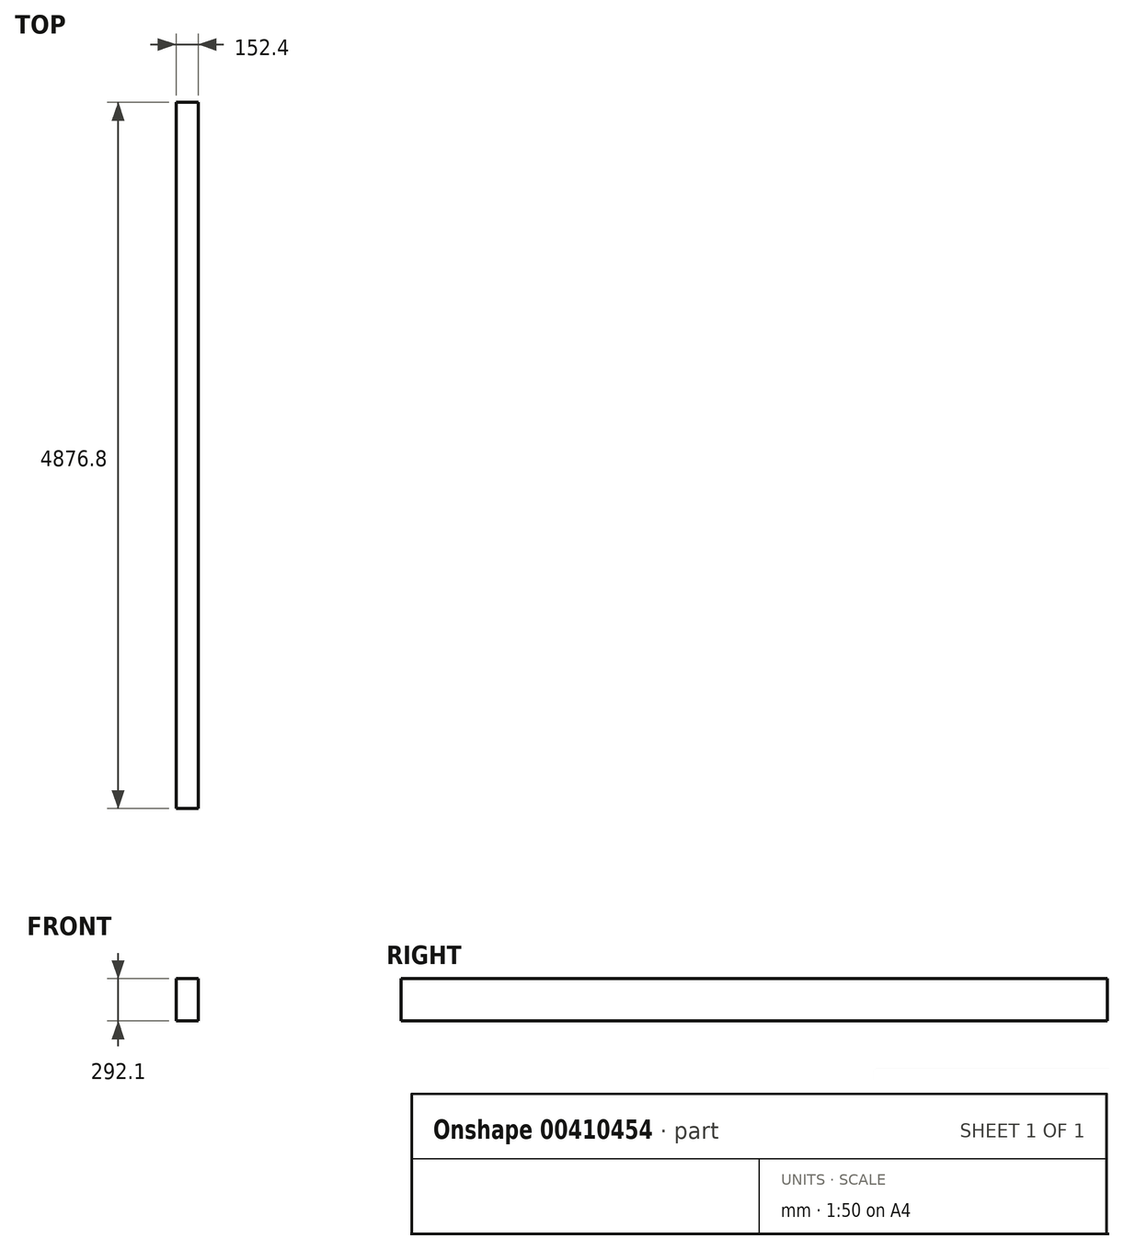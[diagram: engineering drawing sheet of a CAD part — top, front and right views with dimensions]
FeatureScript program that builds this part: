
annotation { "Feature Type Name" : "Feature", "Feature Type Description" : "" }
export const myFeature = defineFeature(function(context is Context, id is Id, definition is map)
    precondition{}
    {
        {
            var Q0;
            Q0=qCreatedBy(makeId("Right.planeOp"),FACE);
            var sketch = newSketch(context, id + "F0", { "sketchPlane" : qUnion([Q0])});
            skLineSegment(sketch, "E0.bottom", {"start": v(-2438.4, 146.05) * mm, "end": v(2438.4, 146.05) * mm});
            skLineSegment(sketch, "E0.top", {"start": v(-2438.4, -146.05) * mm, "end": v(2438.4, -146.05) * mm});
            skLineSegment(sketch, "E0.left", {"start": v(-2438.4, 146.05) * mm, "end": v(-2438.4, -146.05) * mm});
            skLineSegment(sketch, "E0.right", {"start": v(2438.4, 146.05) * mm, "end": v(2438.4, -146.05) * mm});
            skPoint(sketch, "E0.middle", {"position": v(0, 0) * mm});
            skSolve(sketch);
        }
        {
            var Q0;
            Q0=qSketchRegion(id+"F0",true);
            extrude(context, id + "F1", {"entities" : qUnion([Q0]), "depth" : 152.4 * mm, "offsetDistance" : 25.4 * mm});
        }
    });
